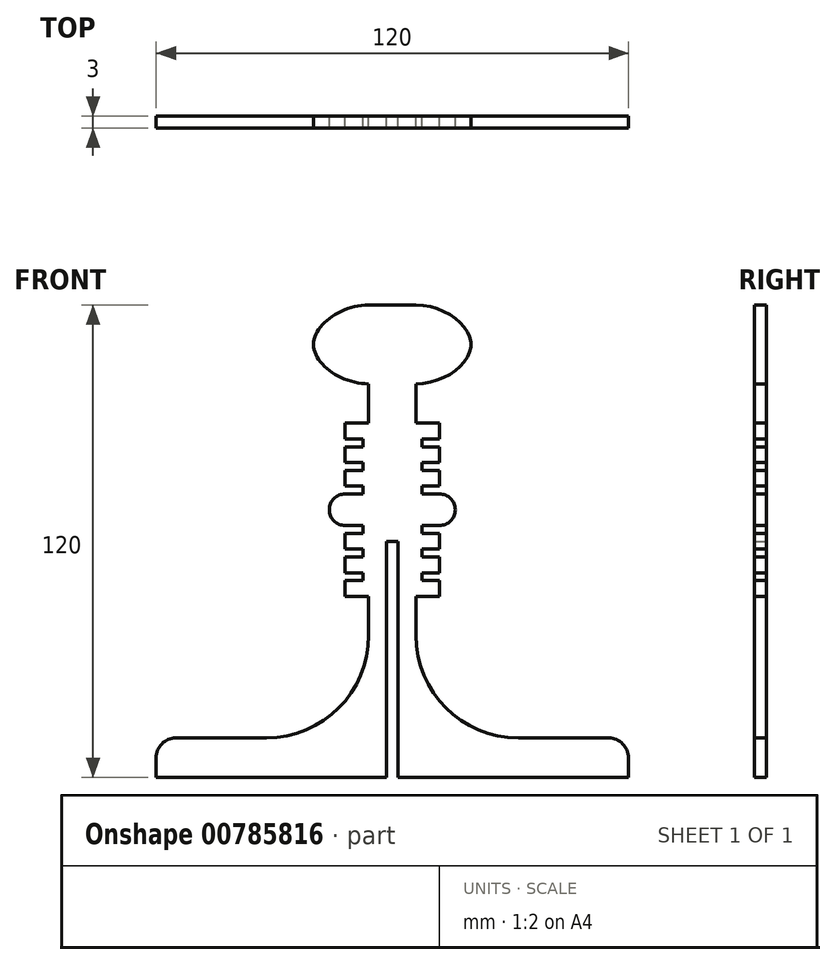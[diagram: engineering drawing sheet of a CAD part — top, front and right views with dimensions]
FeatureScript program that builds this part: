
annotation { "Feature Type Name" : "Feature", "Feature Type Description" : "" }
export const myFeature = defineFeature(function(context is Context, id is Id, definition is map)
    precondition{}
    {
        {
            var Q0;
            Q0=qCreatedBy(makeId("Front.planeOp"),FACE);
            var sketch = newSketch(context, id + "F0", { "sketchPlane" : qUnion([Q0])});
            skLineSegment(sketch, "E0", {"start": v(60, 0) * mm, "end": v(60, 5) * mm});
            skLineSegment(sketch, "E1", {"start": v(55, 10) * mm, "end": v(32, 10) * mm});
            skLineSegment(sketch, "E2", {"start": v(6, 36) * mm, "end": v(6, 100) * mm});
            skLineSegment(sketch, "E3", {"start": v(-6, 100) * mm, "end": v(-6, 36) * mm});
            skLineSegment(sketch, "E4", {"start": v(-32, 10) * mm, "end": v(-55, 10) * mm});
            skLineSegment(sketch, "E5", {"start": v(-60, 5) * mm, "end": v(-60, 0) * mm});
            skLineSegment(sketch, "E6", {"start": v(-1.5, 120) * mm, "end": v(-6, 120) * mm});
            skLineSegment(sketch, "E7", {"start": v(1.5, 120) * mm, "end": v(6, 120) * mm});
            skFitSpline(sketch, "E8", {"points": [v(-6, 120) * mm, v(-20, 110) * mm, v(-6, 100) * mm], "startDerivative": vector(-42.6, 0) * mm, "endDerivative": vector(42.6, 0.15) * mm});
            skLineSegment(sketch, "E9", {"start": v(-20, 110) * mm, "end": v(-6, 110) * mm});
            skLineSegment(sketch, "E10", {"start": v(-6, 100) * mm, "end": v(-1.5, 100) * mm});
            skLineSegment(sketch, "E11", {"start": v(-6, 90) * mm, "end": v(-12, 90) * mm});
            skLineSegment(sketch, "E12", {"start": v(-12, 90) * mm, "end": v(-12, 86) * mm});
            skLineSegment(sketch, "E13", {"start": v(-12, 86) * mm, "end": v(-7.5, 86) * mm});
            skLineSegment(sketch, "E14", {"start": v(-7.5, 86) * mm, "end": v(-7.5, 84) * mm});
            skLineSegment(sketch, "E15", {"start": v(-7.5, 84) * mm, "end": v(-12, 84) * mm});
            skLineSegment(sketch, "E16", {"start": v(-12, 84) * mm, "end": v(-12, 80) * mm});
            skLineSegment(sketch, "E17", {"start": v(-12, 80) * mm, "end": v(-7.5, 80) * mm});
            skLineSegment(sketch, "E18", {"start": v(-7.5, 80) * mm, "end": v(-7.5, 78) * mm});
            skLineSegment(sketch, "E19", {"start": v(-7.5, 78) * mm, "end": v(-12, 78) * mm});
            skLineSegment(sketch, "E20", {"start": v(-12, 78) * mm, "end": v(-12, 74) * mm});
            skLineSegment(sketch, "E21", {"start": v(-12, 74) * mm, "end": v(-7.5, 74) * mm});
            skLineSegment(sketch, "E22", {"start": v(-7.5, 74) * mm, "end": v(-7.5, 72) * mm});
            skLineSegment(sketch, "E23", {"start": v(-7.5, 72) * mm, "end": v(-12, 72) * mm});
            skLineSegment(sketch, "E24", {"start": v(-12, 72) * mm, "end": v(-12, 68) * mm});
            skLineSegment(sketch, "E25", {"start": v(-12, 68) * mm, "end": v(-6, 68) * mm});
            skArc(sketch, "E26", {"start": v(-32, 10) * mm, "mid": v(-13.62, 17.62) * mm, "end": v(-6, 36) * mm});
            skLineSegment(sketch, "E27.MirrorCS", {"start": v(-12, 64) * mm, "end": v(-12, 68) * mm});
            skLineSegment(sketch, "E28.MirrorCS", {"start": v(-7.5, 64) * mm, "end": v(-12, 64) * mm});
            skLineSegment(sketch, "E29.MirrorCS", {"start": v(-7.5, 62) * mm, "end": v(-7.5, 64) * mm});
            skLineSegment(sketch, "E30.MirrorCS", {"start": v(-12, 62) * mm, "end": v(-7.5, 62) * mm});
            skLineSegment(sketch, "E31.MirrorCS", {"start": v(-12, 58) * mm, "end": v(-12, 62) * mm});
            skLineSegment(sketch, "E32.MirrorCS", {"start": v(-7.5, 58) * mm, "end": v(-12, 58) * mm});
            skLineSegment(sketch, "E33.MirrorCS", {"start": v(-7.5, 56) * mm, "end": v(-7.5, 58) * mm});
            skLineSegment(sketch, "E34.MirrorCS", {"start": v(-12, 56) * mm, "end": v(-7.5, 56) * mm});
            skLineSegment(sketch, "E35.MirrorCS", {"start": v(-12, 52) * mm, "end": v(-12, 56) * mm});
            skLineSegment(sketch, "E36.MirrorCS", {"start": v(-7.5, 52) * mm, "end": v(-12, 52) * mm});
            skLineSegment(sketch, "E37.MirrorCS", {"start": v(-7.5, 50) * mm, "end": v(-7.5, 52) * mm});
            skLineSegment(sketch, "E38.MirrorCS", {"start": v(-12, 50) * mm, "end": v(-7.5, 50) * mm});
            skLineSegment(sketch, "E39.MirrorCS", {"start": v(-12, 46) * mm, "end": v(-12, 50) * mm});
            skLineSegment(sketch, "E40.MirrorCS", {"start": v(-6, 46) * mm, "end": v(-12, 46) * mm});
            skPoint(sketch, "E41.visualSharp", {"position": v(-60, 10) * mm});
            skArc(sketch, "E41.filletArc", {"start": v(-55, 10) * mm, "mid": v(-58.54, 8.54) * mm, "end": v(-60, 5) * mm});
            skArc(sketch, "E42.MirrorCS", {"start": v(32, 10) * mm, "mid": v(13.62, 17.62) * mm, "end": v(6, 36) * mm});
            skFitSpline(sketch, "E43.MirrorCS", {"points": [v(6, 120) * mm, v(20, 110) * mm, v(6, 100) * mm], "startDerivative": vector(42.6, 0) * mm, "endDerivative": vector(-42.6, 0.15) * mm});
            skLineSegment(sketch, "E44.MirrorCS", {"start": v(6, 46) * mm, "end": v(12, 46) * mm});
            skLineSegment(sketch, "E45.MirrorCS", {"start": v(12, 46) * mm, "end": v(12, 50) * mm});
            skLineSegment(sketch, "E46.MirrorCS", {"start": v(12, 50) * mm, "end": v(7.5, 50) * mm});
            skLineSegment(sketch, "E47.MirrorCS", {"start": v(7.5, 50) * mm, "end": v(7.5, 52) * mm});
            skLineSegment(sketch, "E48.MirrorCS", {"start": v(7.5, 52) * mm, "end": v(12, 52) * mm});
            skLineSegment(sketch, "E49.MirrorCS", {"start": v(12, 52) * mm, "end": v(12, 56) * mm});
            skLineSegment(sketch, "E50.MirrorCS", {"start": v(12, 56) * mm, "end": v(7.5, 56) * mm});
            skLineSegment(sketch, "E51.MirrorCS", {"start": v(7.5, 56) * mm, "end": v(7.5, 58) * mm});
            skLineSegment(sketch, "E52.MirrorCS", {"start": v(7.5, 58) * mm, "end": v(12, 58) * mm});
            skLineSegment(sketch, "E53.MirrorCS", {"start": v(12, 58) * mm, "end": v(12, 62) * mm});
            skLineSegment(sketch, "E54.MirrorCS", {"start": v(12, 62) * mm, "end": v(7.5, 62) * mm});
            skLineSegment(sketch, "E55.MirrorCS", {"start": v(7.5, 62) * mm, "end": v(7.5, 64) * mm});
            skLineSegment(sketch, "E56.MirrorCS", {"start": v(7.5, 64) * mm, "end": v(12, 64) * mm});
            skLineSegment(sketch, "E57.MirrorCS", {"start": v(12, 64) * mm, "end": v(12, 68) * mm});
            skLineSegment(sketch, "E58.MirrorCS", {"start": v(12, 72) * mm, "end": v(12, 68) * mm});
            skLineSegment(sketch, "E59.MirrorCS", {"start": v(7.5, 72) * mm, "end": v(12, 72) * mm});
            skLineSegment(sketch, "E60.MirrorCS", {"start": v(7.5, 74) * mm, "end": v(7.5, 72) * mm});
            skLineSegment(sketch, "E61.MirrorCS", {"start": v(12, 74) * mm, "end": v(7.5, 74) * mm});
            skLineSegment(sketch, "E62.MirrorCS", {"start": v(12, 78) * mm, "end": v(12, 74) * mm});
            skLineSegment(sketch, "E63.MirrorCS", {"start": v(7.5, 78) * mm, "end": v(12, 78) * mm});
            skLineSegment(sketch, "E64.MirrorCS", {"start": v(7.5, 80) * mm, "end": v(7.5, 78) * mm});
            skLineSegment(sketch, "E65.MirrorCS", {"start": v(12, 80) * mm, "end": v(7.5, 80) * mm});
            skLineSegment(sketch, "E66.MirrorCS", {"start": v(12, 84) * mm, "end": v(12, 80) * mm});
            skLineSegment(sketch, "E67.MirrorCS", {"start": v(7.5, 84) * mm, "end": v(12, 84) * mm});
            skLineSegment(sketch, "E68.MirrorCS", {"start": v(7.5, 86) * mm, "end": v(7.5, 84) * mm});
            skLineSegment(sketch, "E69.MirrorCS", {"start": v(12, 86) * mm, "end": v(7.5, 86) * mm});
            skLineSegment(sketch, "E70.MirrorCS", {"start": v(12, 90) * mm, "end": v(12, 86) * mm});
            skLineSegment(sketch, "E71.MirrorCS", {"start": v(6, 90) * mm, "end": v(12, 90) * mm});
            skPoint(sketch, "E72.visualSharp", {"position": v(60, 0) * mm});
            skPoint(sketch, "E73.visualSharp", {"position": v(60, 10) * mm});
            skArc(sketch, "E73.filletArc", {"start": v(60, 5) * mm, "mid": v(58.54, 8.54) * mm, "end": v(55, 10) * mm});
            skArc(sketch, "E74", {"start": v(-12, 72) * mm, "mid": v(-16, 68) * mm, "end": v(-12, 64) * mm});
            skArc(sketch, "E75.MirrorCS", {"start": v(12, 72) * mm, "mid": v(16, 68) * mm, "end": v(12, 64) * mm});
            skLineSegment(sketch, "E76", {"start": v(-1.5, 120) * mm, "end": v(1.5, 120) * mm});
            skLineSegment(sketch, "E77", {"start": v(-1.5, 120) * mm, "end": v(-1.5, 100) * mm});
            skLineSegment(sketch, "E78", {"start": v(-60, 0) * mm, "end": v(-1.5, 0) * mm});
            skLineSegment(sketch, "E79", {"start": v(-1.5, 0) * mm, "end": v(-1.5, 60) * mm});
            skLineSegment(sketch, "E80", {"start": v(-1.5, 60) * mm, "end": v(1.5, 60) * mm});
            skLineSegment(sketch, "E81", {"start": v(1.5, 60) * mm, "end": v(1.5, 0) * mm});
            skLineSegment(sketch, "E82", {"start": v(1.5, 0) * mm, "end": v(60, 0) * mm});
            skSolve(sketch);
        }
        {
            var Q0;
            Q0=makeQuery(id+"F0.imprint","IMPRINT",FACE,{"disambiguationData":[TD([[makeQuery(id+"F0.imprint","IMPRINT",EDGE,{"derivedFrom":sQuery(id+"F0.wireOp",EDGE,"OrIbVIw1-cZfK-JwsD-GHKV-li3u5z8OHSWb")}),1.0]])]});
            var Q1;
            {var subQ1=sQuery(id+"F0.wireOp",EDGE,"E6");Q1=makeQuery(id+"F0.imprint","IMPRINT",FACE,{"disambiguationData":[TD([[makeQuery(id+"F0.imprint","IMPRINT",EDGE,{"derivedFrom":subQ1}),1.0]])]});}
            var Q2;
            {var subQ0=sQuery(id+"F0.wireOp",EDGE,"E11");Q2=makeQuery(id+"F0.imprint","IMPRINT",FACE,{"disambiguationData":[TD([[makeQuery(id+"F0.imprint","IMPRINT",EDGE,{"derivedFrom":subQ0}),1.0]])]});}
            var Q3;
            {var subQ0=sQuery(id+"F0.wireOp",EDGE,"E25");Q3=makeQuery(id+"F0.imprint","IMPRINT",FACE,{"disambiguationData":[TD([[makeQuery(id+"F0.imprint","IMPRINT",EDGE,{"derivedFrom":subQ0}),-1.0]])]});}
            var Q4;
            Q4=makeQuery(id+"F0.imprint","IMPRINT",FACE,{"disambiguationData":[TD([[makeQuery(id+"F0.imprint","IMPRINT",EDGE,{"derivedFrom":sQuery(id+"F0.wireOp",EDGE,"E24")}),-1.0]])]});
            var Q5;
            Q5=makeQuery(id+"F0.imprint","IMPRINT",FACE,{"disambiguationData":[TD([[makeQuery(id+"F0.imprint","IMPRINT",EDGE,{"derivedFrom":sQuery(id+"F0.wireOp",EDGE,"E57.MirrorCS")}),-1.0]])]});
            var Q6;
            {var subQ0=sQuery(id+"F0.wireOp",EDGE,"E44.MirrorCS");Q6=makeQuery(id+"F0.imprint","IMPRINT",FACE,{"disambiguationData":[TD([[makeQuery(id+"F0.imprint","IMPRINT",EDGE,{"derivedFrom":subQ0}),1.0]])]});}
            var Q7;
            Q7=makeQuery(id+"F0.imprint","IMPRINT",FACE,{"disambiguationData":[TD([[makeQuery(id+"F0.imprint","IMPRINT",EDGE,{"derivedFrom":sQuery(id+"F0.wireOp",EDGE,"E0")}),1.0]])]});
            extrude(context, id + "F1", {"entities" : qUnion([Q0, Q1, Q2, Q3, Q4, Q5, Q6, Q7]), "depth" : 3 * mm, "offsetDistance" : 25 * mm});
        }
    });
